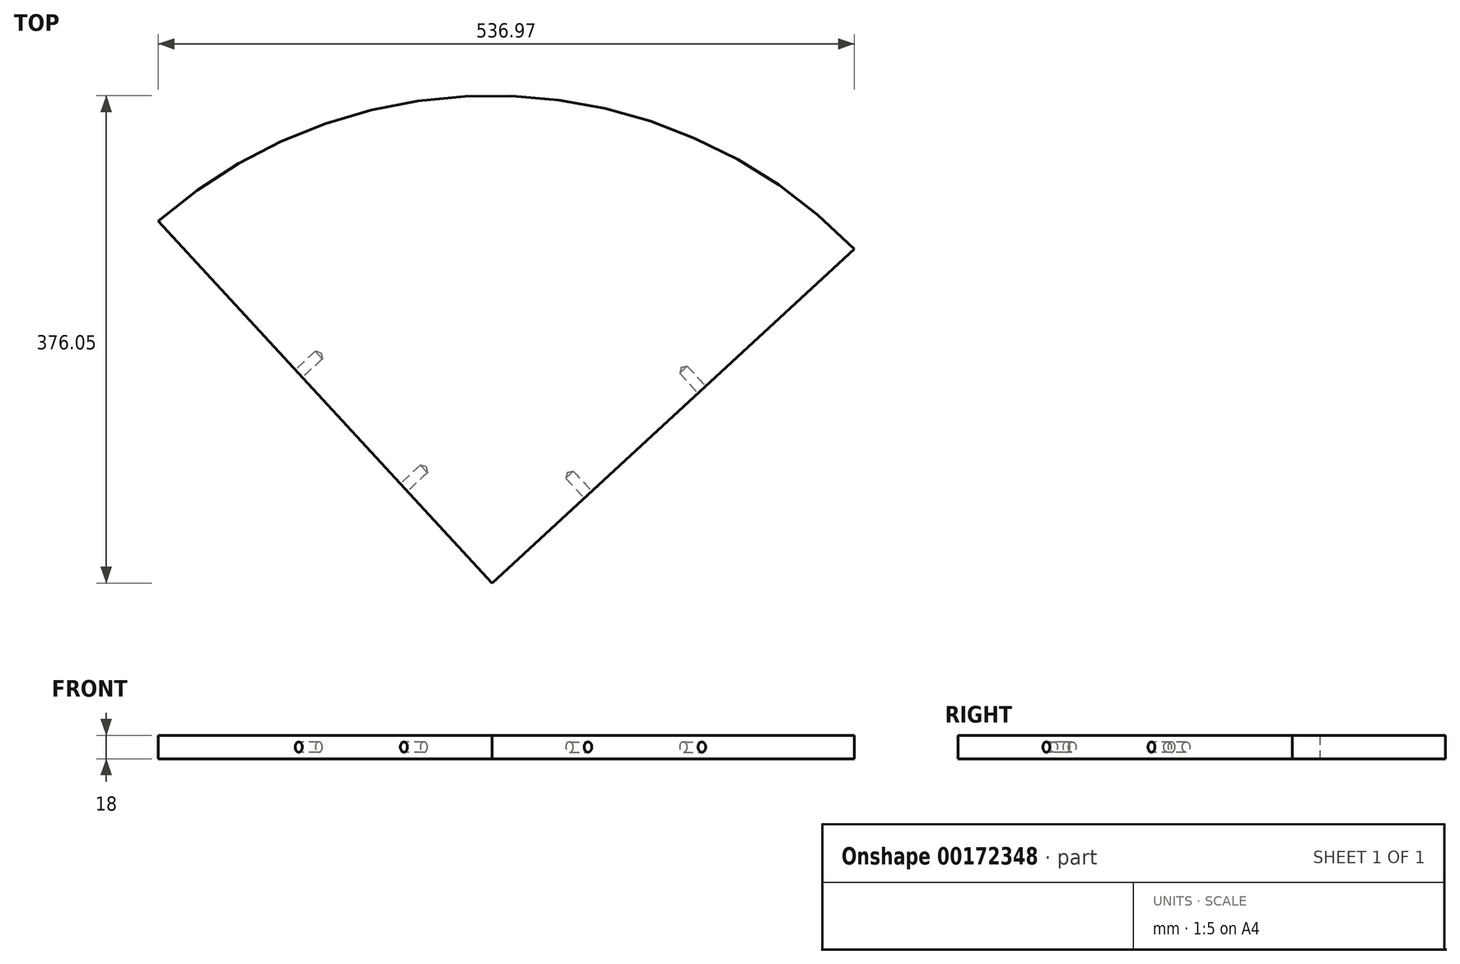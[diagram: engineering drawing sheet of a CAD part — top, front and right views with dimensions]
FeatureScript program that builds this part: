
annotation { "Feature Type Name" : "Feature", "Feature Type Description" : "" }
export const myFeature = defineFeature(function(context is Context, id is Id, definition is map)
    precondition{}
    {
        {
            var Q0;
            Q0=qCreatedBy(makeId("Top.planeOp"),FACE);
            var sketch = newSketch(context, id + "F0", { "sketchPlane" : qUnion([Q0])});
            skArc(sketch, "E0", {"start": v(-260.15, 290.55) * mm, "mid": v(21.5, 389.4) * mm, "end": v(290.55, 260.15) * mm});
            skLineSegment(sketch, "E1", {"start": v(-260.15, 290.55) * mm, "end": v(0, 0) * mm});
            skLineSegment(sketch, "E2", {"start": v(290.55, 260.15) * mm, "end": v(0, 0) * mm});
            skLineSegment(sketch, "E3", {"start": v(-257.21, 293.16) * mm, "end": v(0.56, 13.95) * mm});
            skLineSegment(sketch, "E4", {"start": v(0.56, 13.95) * mm, "end": v(279.76, 271.72) * mm});
            skSolve(sketch);
        }
        {
            var Q0;
            {var subQ0=sQuery(id+"F0.wireOp",EDGE,"E3");Q0=makeQuery(id+"F0.imprint","IMPRINT",FACE,{"disambiguationData":[TD([[makeQuery(id+"F0.imprint","IMPRINT",EDGE,{"derivedFrom":subQ0}),1.0]])]});}
            extrude(context, id + "F1", {"entities" : qUnion([Q0]), "depth" : 18 * mm});
        }
        {
            var Q0;
            Q0=makeQuery(id+"F1.opExtrude","SWEPT_FACE",FACE,{"disambiguationData":[OSD([sQuery(id+"F0.wireOp",EDGE,"E3")])]});
            var sketch = newSketch(context, id + "F2", { "sketchPlane" : qUnion([Q0])});
            skPoint(sketch, "E5", {"position": v(-229.87, 9) * mm});
            skPoint(sketch, "E6", {"position": v(-110.37, 9) * mm});
            skSolve(sketch);
        }
        {
            var Q0;
            Q0=makeQuery(id+"F1.opExtrude","SWEPT_FACE",FACE,{"disambiguationData":[OSD([sQuery(id+"F0.wireOp",EDGE,"E4")])]});
            var sketch = newSketch(context, id + "F3", { "sketchPlane" : qUnion([Q0])});
            skPoint(sketch, "E7", {"position": v(110.37, 9) * mm});
            skPoint(sketch, "E8", {"position": v(229.87, 9) * mm});
            skSolve(sketch);
        }
        {
            var Q0;
            Q0=sQuery(id+"F3.wireOp",VERTEX,"E7");
            var Q1;
            Q1=sQuery(id+"F3.wireOp",VERTEX,"E8");
            var Q2;
            Q2=sQuery(id+"F2.wireOp",VERTEX,"E6");
            var Q3;
            Q3=sQuery(id+"F2.wireOp",VERTEX,"E5");
            var Q4;
            Q4=makeQuery(id+"F1.opExtrude","SWEPT_BODY",BODY,{"disambiguationData":[OSD([sQuery(id+"F0.wireOp",EDGE,"E0"),sQuery(id+"F0.wireOp",EDGE,"E1"),sQuery(id+"F0.wireOp",EDGE,"E2")])]});
            hole(context, id + "F4", {"style" : HoleStyle.SIMPLE, "endStyle" : HoleEndStyle.BLIND, "holeDiameter" : 8 * mm, "holeDepth" : 21 * mm, "startFromSketch" : true, "locations" : qUnion([Q0, Q1, Q2, Q3]), "scope" : qUnion([Q4])});
        }
    });
